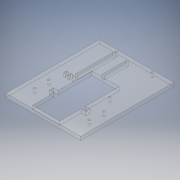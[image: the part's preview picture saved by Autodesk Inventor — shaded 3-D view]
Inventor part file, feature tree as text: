
AUTODESK INVENTOR PART (.ipt)
format: ipt  version: 2018 (Build 220112000, 112)  size: 190,464 bytes
history: native  units: in
note: dims shown in document units (in); Inventor stores cm internally (conversion verified against a paired STEP export)
features: sketch x7, other x5, hole x2, sheet_metal_op x1
ambient origin geometry x8: Origin, YZ Plane, XZ Plane, XY Plane, X Axis, Y Axis, Z Axis, Center Point
bodies: Solid1 (feature_tree)
feature tree (15):
  sheet_metal_op  "Face1"
  hole  "MotorScrews"  [1 undecoded]
  hole  "PiScrews"  [1 undecoded]
  sketch  "Sketch1"  dims[d0=4.0in d1=5.0in]
  other  "Plate1"
  sketch  "Sketch2"  dims[d4=0.2in d5=0.77in]
  sketch  "Sketch3"  dims[d6=0.53in]
  sketch  "Sketch4"  dims[d7=0.129in d8=0.75in d9=0.279in d10=0.188in d11=0.5635in d12=0.2in]
  sketch  "Sketch5"  dims[d13=0.8108in]
  sketch  "Sketch6"  dims[d14=1.4567in]
  sketch  "Sketch7"  dims[d15=3.189in d16=0.2in d17=0.0in d18=1.0in d19=0.2in d20=0.0in d21=1.0in d22=1.929in d23=2.283in d24=0.125in d25=0.114in d26=0.75in d27=0.217in d28=0.25in d29=90.0deg d30=0.2in d31=0.8108in d33=0.125in d34=2.0in d35=0.2in d36=0.0in d37=0.6in d38=0.1in d39=0.15in d40=0.1in d41=0.15in d42=0.2in d43=0.0in]
  other  "BatteryHole"
  other  "MotorWireHoles"
  other  "WireHoles"
  other  "ZipTieHolder"
note: 2 required parameter values undecoded (feature->parameter linkage not recoverable at this tier; creation-order binding heuristic only, values carry confidence <= 0.55)
